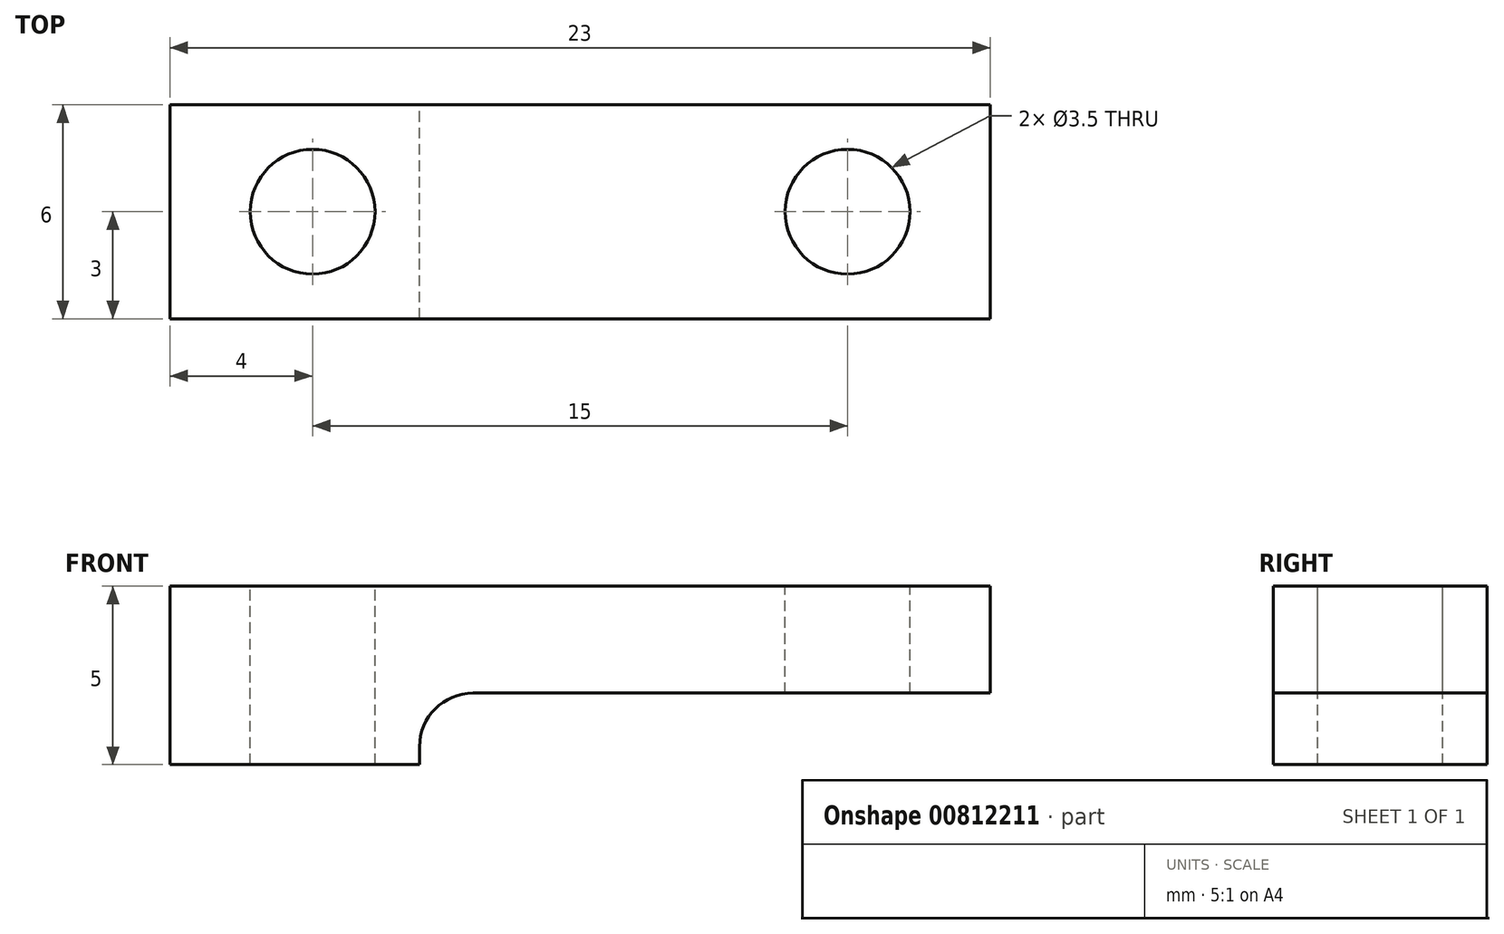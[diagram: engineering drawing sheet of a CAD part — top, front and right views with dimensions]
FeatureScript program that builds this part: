
annotation { "Feature Type Name" : "Feature", "Feature Type Description" : "" }
export const myFeature = defineFeature(function(context is Context, id is Id, definition is map)
    precondition{}
    {
        {
            var Q0;
            Q0=qCreatedBy(makeId("Front.planeOp"),FACE);
            var sketch = newSketch(context, id + "F0", { "sketchPlane" : qUnion([Q0])});
            skLineSegment(sketch, "E0.bottom", {"start": v(5, 5) * mm, "end": v(28, 5) * mm});
            skLineSegment(sketch, "E0.top", {"start": v(5, 8) * mm, "end": v(28, 8) * mm});
            skLineSegment(sketch, "E0.left", {"start": v(5, 5) * mm, "end": v(5, 8) * mm});
            skLineSegment(sketch, "E0.right", {"start": v(28, 5) * mm, "end": v(28, 8) * mm});
            skLineSegment(sketch, "E1.bottom", {"start": v(28, 5) * mm, "end": v(21, 5) * mm});
            skLineSegment(sketch, "E1.top", {"start": v(28, 3) * mm, "end": v(21, 3) * mm});
            skLineSegment(sketch, "E1.left", {"start": v(28, 5) * mm, "end": v(28, 3) * mm});
            skLineSegment(sketch, "E1.right", {"start": v(21, 5) * mm, "end": v(21, 3) * mm});
            skLineSegment(sketch, "E2", {"start": v(16.5, 14.13) * mm, "end": v(16.5, -3.83) * mm, "construction": true});
            skPoint(sketch, "E2.startSnap0", {"position": v(16.5, 8) * mm});
            skPoint(sketch, "E2.endSnap0", {"position": v(16.5, 5) * mm});
            skLineSegment(sketch, "E3.MirrorCS", {"start": v(5, 3) * mm, "end": v(12, 3) * mm});
            skLineSegment(sketch, "E4.MirrorCS", {"start": v(12, 5) * mm, "end": v(12, 3) * mm});
            skLineSegment(sketch, "E5.MirrorCS", {"start": v(5, 5) * mm, "end": v(5, 3) * mm});
            skLineSegment(sketch, "E6", {"start": v(16.5, 14.13) * mm, "end": v(24, 14.13) * mm, "construction": true});
            skLineSegment(sketch, "E7", {"start": v(24, 14.13) * mm, "end": v(24, -6.13) * mm, "construction": true});
            skSolve(sketch);
        }
        {
            var Q0;
            Q0=makeQuery(id+"F0.imprint","IMPRINT",FACE,{"disambiguationData":[TD([[makeQuery(id+"F0.imprint","IMPRINT",EDGE,{"derivedFrom":sQuery(id+"F0.wireOp",EDGE,"E0.top")}),-1.0]])]});
            var Q1;
            Q1=makeQuery(id+"F0.imprint","IMPRINT",FACE,{"disambiguationData":[TD([[makeQuery(id+"F0.imprint","IMPRINT",EDGE,{"derivedFrom":sQuery(id+"F0.wireOp",EDGE,"E3.MirrorCS")}),1.0]])]});
            var Q2;
            Q2=makeQuery(id+"F0.imprint","IMPRINT",FACE,{"disambiguationData":[TD([[makeQuery(id+"F0.imprint","IMPRINT",EDGE,{"derivedFrom":sQuery(id+"F0.wireOp",EDGE,"E1.bottom")}),1.0]])]});
            extrude(context, id + "F1", {"entities" : qUnion([Q0, Q1, Q2]), "depth" : 6 * mm, "offsetDistance" : 25 * mm});
        }
        {
            var Q0;
            Q0=makeQuery(id+"F1.opExtrude","SWEPT_FACE",FACE,{"disambiguationData":[OSD([sQuery(id+"F0.wireOp",EDGE,"E0.top")])]});
            var sketch = newSketch(context, id + "F2", { "sketchPlane" : qUnion([Q0])});
            skLineSegment(sketch, "E8", {"start": v(3.84, -3) * mm, "end": v(29.75, -3) * mm, "construction": true});
            skPoint(sketch, "E8.startSnap0", {"position": v(5, -3) * mm});
            skLineSegment(sketch, "E9", {"start": v(16.5, 1.24) * mm, "end": v(16.5, -9.2) * mm, "construction": true});
            skPoint(sketch, "E9.startSnap0", {"position": v(16.5, 0) * mm});
            skLineSegment(sketch, "E10.0", {"start": v(9, 1.24) * mm, "end": v(9, -9.2) * mm, "construction": true});
            skLineSegment(sketch, "E11.MirrorCS", {"start": v(24, 1.24) * mm, "end": v(24, -9.2) * mm, "construction": true});
            skCircle(sketch, "E12", {"center": v(9, -3) * mm, "radius": 1.75 * mm});
            skCircle(sketch, "E13", {"center": v(24, -3) * mm, "radius": 1.75 * mm});
            skSolve(sketch);
        }
        {
            var Q0;
            Q0=makeQuery(id+"F2.imprint","IMPRINT",FACE,{"disambiguationData":[TD([[makeQuery(id+"F2.imprint","IMPRINT",EDGE,{"derivedFrom":sQuery(id+"F2.wireOp",EDGE,"E12")}),1.0]])]});
            var Q1;
            Q1=makeQuery(id+"F2.imprint","IMPRINT",FACE,{"disambiguationData":[TD([[makeQuery(id+"F2.imprint","IMPRINT",EDGE,{"derivedFrom":sQuery(id+"F2.wireOp",EDGE,"E13")}),1.0]])]});
            extrude(context, id + "F3", {"entities" : qUnion([Q0, Q1]), "operationType" : NewBodyOperationType.REMOVE, "endBound" : BoundingType.THROUGH_ALL, "oppositeDirection" : true, "depth" : 25 * mm, "offsetDistance" : 25 * mm});
        }
        {
            var Q0;
            Q0=makeQuery(id+"F1.opExtrude","SWEPT_EDGE",EDGE,{"disambiguationData":[OSD([sQuery(id+"F0.wireOp",EDGE,"E0.bottom"),sQuery(id+"F0.wireOp",EDGE,"E4.MirrorCS")])]});
            var Q1;
            Q1=makeQuery(id+"F1.opExtrude","SWEPT_EDGE",EDGE,{"disambiguationData":[OSD([sQuery(id+"F0.wireOp",EDGE,"E0.bottom"),sQuery(id+"F0.wireOp",EDGE,"E1.bottom"),sQuery(id+"F0.wireOp",EDGE,"E1.right")])]});
            fillet(context, id + "F4", {"entities" : qUnion([Q0, Q1]), "radius" : 1.5 * mm, "tangentPropagation" : true, "allowEdgeOverflow" : false});
        }
    });
